# Revit family: Hager-FW-Surface_mounted-IP30-With_Cover-With_DIN-Hosted-ES-es
name_source: partatom
category: Electrical Equipment
units: mm (PartAtom-declared; Revit-internal decimal feet)

## family parameters
Cut with Voids When Loaded = No
Host = Face
Maintain Annotation Orientation = Yes
Panel Configuration = Two Columns, Circuits Across
Part Type = Panelboard
Room Calculation Point = No
Round Connector Dimension = Use Diameter
Shared = No

## types (12) — shared parameters
BC_MODEL_ID = 1554233
BC_OBJECT_ID = 513835
BC_OBJECT_VERSION = #3
Code hager = ADD-EC000214_EU
EF000003 - Método de montaje = Montado superficial (escayola)
EF000007 - Color = Blanco
EF000024 - Resistente a UV = No
EF000049 - Profundidad = 150 mm
EF000116 - Número RAL = 9010
EF000118 - Con placa de montaje = No
EF001062 - Versión de CEM = No
EF001088 - Posibilidad de extensión = Yes
EF001134 - Carril DIN = Yes
EF004462 - Tipo de cierre = Otros
EF005474 - Grado de protección (IP) = IP30
EF006244 - Tapa/puerta transparente = No
EF006306 - Con candado = No
EF009212 - Versión de la cubierta = Cerrado
EF015776 - Borne de tierra = Yes
EF015777 - Borne neutro = No
EF015941 - Puerta de transmisión de señal = No
ETIM class code = EC000214
ETIM class name = Small distribution board
HG000001 - Número de columnas = 1
HG000002-with door or cover-es = Yes
HG000003-Range-es = FW
HG000005-Thickness-es = 2 mm  [stored 0.00656168 ft]
HG000006-Flush mounted-es = No
HG000009-Double swing door-es = No
HG000010-Asymmetric doors-es = No
HG000011-Empty rows from bottom-es = No
HG000012-Door swing angle-es = 90.00°
HG000013-Door on the left-es = No
HG000014-Door on the right-es = Yes
HG000015-Clearance visibility-es = Yes
HG000016-Door 3D visibility-es = Yes
HG000017-Distance between poles-es = 18 mm  [stored 0.0590551 ft]
HG000060-RAL-number = 9010
HG000099-Onfly Template ID-es-ES = 507532
Manufacturer = Hager
Name = FW-Surface_mounted-IP30-With_Cover-With_DIN-ES
Name BIM&CO = Electricity
Name hager = ADD_Enclosures_EC000214
Uniformat = Low Tension Service & Dist.
Uniformat code = D501001
zero-valued in all types: Default Elevation, EF000218 - Profundidad de instalación, EF000332 - Altura de la instalación, EF000846 - Anchura de montaje, EF001131 - Profundidad interna, HG000007-Number of empty columns-es, HG000008-Number of empty rows-es

## per-type parameters (varying)
| type | BC_VARIANT_ID | EF000008 - Anchura | EF000040 - Altura | EF000266 - Número de filas | EF002950 - Ancho en número de espacios modulares | HG000004-Manufacturer reference-es | HGEF000266-Número de filas | HGEF0002950-Ancho en número de espacios modulares |
| FW-Surface_mounted_W355_H641_D150_12_Modular_Spacing-FW312WT | 1178742 | 355 mm | 641 mm  [stored 2.10302 ft] | 3 | 12 | FW312WT | 3 | 12 |
| FW-Surface_mounted_W571_H641_D150_24_Modular_Spacing-FW324WT | 1178743 | 571 mm  [stored 1.87336 ft] | 641 mm  [stored 2.10302 ft] | 3 | 24 | FW324WT | 3 | 24 |
| FW-Surface_mounted_W355_H791_D150_12_Modular_Spacing-FW412WT | 1178744 | 355 mm | 791 mm | 4 | 12 | FW412WT | 4 | 12 |
| FW-Surface_mounted_W571_H791_D150_24_Modular_Spacing-FW424WT | 1178745 | 571 mm  [stored 1.87336 ft] | 791 mm | 4 | 24 | FW424WT | 4 | 24 |
| FW-Surface_mounted_W787_H791_D150_36_Modular_Spacing-FW436WT | 1178746 | 787 mm  [stored 2.58202 ft] | 791 mm | 4 | 36 | FW436WT | 4 | 36 |
| FW-Surface_mounted_W355_H941_D150_12_Modular_Spacing-FW512WT | 1178747 | 355 mm | 941 mm | 5 | 12 | FW512WT | 5 | 12 |
| FW-Surface_mounted_W571_H941_D150_24_Modular_Spacing-FW524WT | 1178748 | 571 mm  [stored 1.87336 ft] | 941 mm | 5 | 24 | FW524WT | 5 | 24 |
| FW-Surface_mounted_W787_H941_D150_36_Modular_Spacing-FW536WT | 1178749 | 787 mm  [stored 2.58202 ft] | 941 mm | 5 | 36 | FW536WT | 5 | 36 |
| FW-Surface_mounted_W355_H1091_D150_12_Modular_Spacing-FW612WT | 1178750 | 355 mm | 1091 mm | 6 | 12 | FW612WT | 6 | 12 |
| FW-Surface_mounted_W571_H1091_D150_24_Modular_Spacing-FW624WT | 1178751 | 571 mm  [stored 1.87336 ft] | 1091 mm | 6 | 24 | FW624WT | 6 | 24 |
| FW-Surface_mounted_W787_H1091_D150_36_Modular_Spacing-FW636WT | 1178753 | 787 mm  [stored 2.58202 ft] | 1091 mm | 6 | 36 | FW636WT | 6 | 36 |
| FW-Surface_mounted_W787_H1241_D150_36_Modular_Spacing-FW736WT | 1178754 | 787 mm  [stored 2.58202 ft] | 1241 mm  [stored 4.07152 ft] | 7 | 36 | FW736WT | 7 | 36 |

note: column(s) folded — value = type name in every type: Reference

note: [stored X ft] marks values corroborated as IEEE doubles in the binary element streams (Revit-internal decimal feet)

## geometry (parser evidence)
native form markers: Sweep x16
no freeform markers — native parametric forms only
